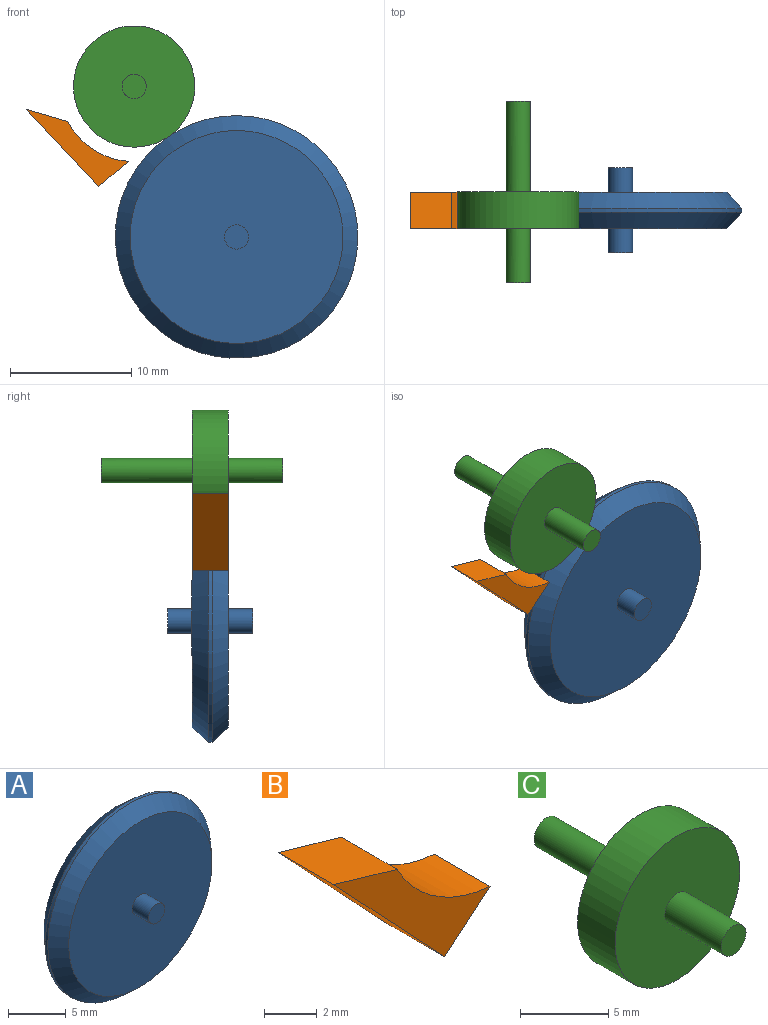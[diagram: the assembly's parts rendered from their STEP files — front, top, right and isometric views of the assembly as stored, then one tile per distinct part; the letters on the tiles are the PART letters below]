
ASSEMBLY  parts=3 mates=3
PART A: 9 faces, bbox 20x7x20 mm
  f0: cone r=10mm half-angle=42.2deg, axis (0,1,0), area 107.5mm2, adj f1,f8
  f1: cylinder r=10mm len=20mm, axis (0,1,0), area 18.8mm2, adj f0,f2
  f2: cone r=10mm half-angle=41.6deg, axis (0,-1,0), area 106.6mm2, adj f1,f3
  f3: plane 17.61x17.61mm, normal (0,1,0), area 240.3mm2, adj f2,f4
  f4: cylinder r=1mm len=2mm, axis (0,1,0), area 12.6mm2, adj f3,f5
  f5: plane 2x2mm, normal (0,1,0), area 3.1mm2, adj f4
  f6: plane 2x2mm, normal (0,-1,0), area 3.1mm2, adj f7
  f7: cylinder r=1mm len=2mm, axis (0,1,0), area 12.6mm2, adj f6,f8
  f8: plane 17.55x17.55mm, normal (0,-1,0), area 238.8mm2, adj f0,f7
PART B: 6 faces, bbox 8.4x3x6.4 mm
  f0: plane 3.42x3mm, normal (0.28,0,0.96), area 10.7mm2, adj f1,f3,f4,f5
  f1: cylinder r=6.19mm len=5mm, axis (0,1,0), area 18.8mm2, adj f0,f2,f4,f5
  f2: plane 3x2.44mm, normal (0.65,0,-0.76), area 9.6mm2, adj f1,f3,f4,f5
  f3: plane 6.35x5.98mm, normal (-0.73,0,-0.69), area 26.2mm2, adj f0,f2,f4,f5
  f4: plane 8.42x6.35mm, normal (0,-1,0), area 13.9mm2, adj f0,f1,f2,f3
  f5: plane 8.42x6.35mm, normal (0,1,0), area 13.9mm2, adj f0,f1,f2,f3
PART C: 7 faces, bbox 10x15x10 mm
  f0: cylinder r=5mm len=10mm, axis (0,1,0), area 94.2mm2, adj f1,f2
  f1: plane 10x10mm, normal (0,-1,0), area 75.4mm2, adj f0,f5
  f2: plane 10x10mm, normal (0,1,0), area 75.4mm2, adj f0,f4
  f3: plane 2x2mm, normal (0,1,0), area 3.1mm2, adj f4
  f4: cylinder r=1mm len=7.5mm, axis (0,-1,0), area 47.1mm2, adj f2,f3
  f5: cylinder r=1mm len=4.5mm, axis (0,-1,0), area 28.3mm2, adj f1,f6
  f6: plane 2x2mm, normal (0,-1,0), area 3.1mm2, adj f5
PLACE A t=(1.98,-5.36,-31.77)mm
PLACE B t=(-6.46,-5.36,-4.37)mm
PLACE C t=(-6.46,-5.36,-4.37)mm
MATE planar C.f0 <-> B.f5  axis (0,1,0) through (-6.46,-5.36,-4.37)mm
MATE cylindrical C.f0 <-> B.f1  axis (0,1,0) through (-6.46,-8.36,-4.37)mm
MATE planar A.f0 <-> C.f0  axis (0,-1,0) through (1.98,-8.36,-16.77)mm
